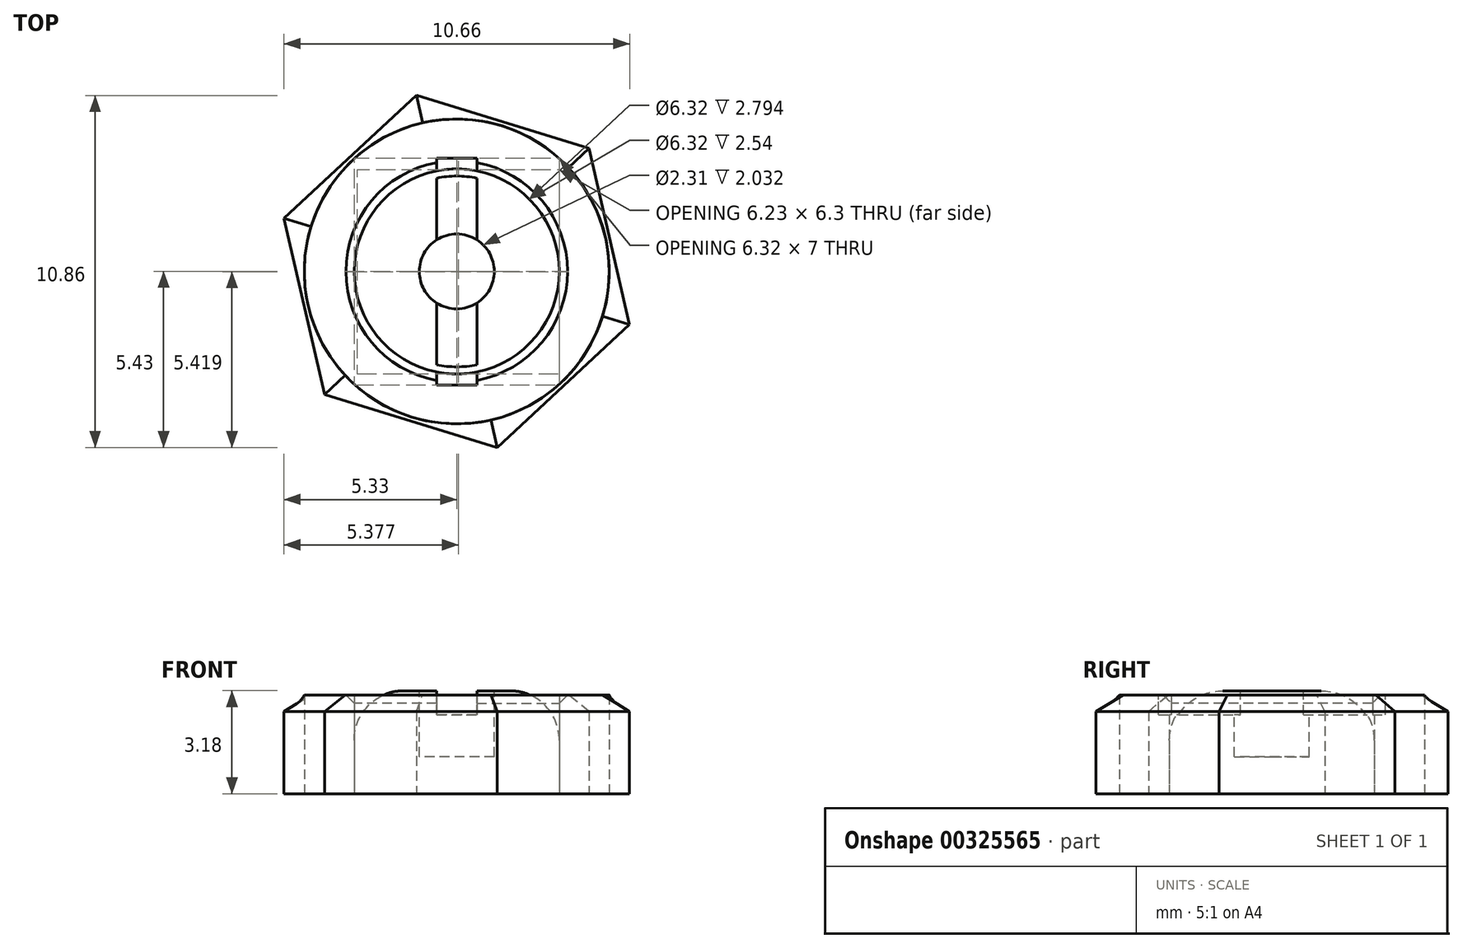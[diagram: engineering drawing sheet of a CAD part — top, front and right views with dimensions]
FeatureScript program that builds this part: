
annotation { "Feature Type Name" : "Feature", "Feature Type Description" : "" }
export const myFeature = defineFeature(function(context is Context, id is Id, definition is map)
    precondition{}
    {
        {
            var Q0;
            Q0=qCreatedBy(makeId("Top.planeOp"),FACE);
            var sketch = newSketch(context, id + "F0", { "sketchPlane" : qUnion([Q0])});
            skCircle(sketch, "E0.cCircle", {"center": v(0, 0) * mm, "radius": 4.83 * mm, "construction": true});
            skLineSegment(sketch, "E0.0", {"start": v(5.33, -1.63) * mm, "end": v(1.25, -5.43) * mm});
            skLineSegment(sketch, "E0.1", {"start": v(1.25, -5.43) * mm, "end": v(-4.08, -3.8) * mm});
            skLineSegment(sketch, "E0.2", {"start": v(-4.08, -3.8) * mm, "end": v(-5.33, 1.63) * mm});
            skLineSegment(sketch, "E0.3", {"start": v(-5.33, 1.63) * mm, "end": v(-1.25, 5.43) * mm});
            skLineSegment(sketch, "E0.4", {"start": v(-1.25, 5.43) * mm, "end": v(4.08, 3.8) * mm});
            skLineSegment(sketch, "E0.5", {"start": v(4.08, 3.8) * mm, "end": v(5.33, -1.63) * mm});
            skPoint(sketch, "E0.0.midPoint", {"position": v(3.29, -3.53) * mm});
            skSolve(sketch);
        }
        {
            var Q0;
            Q0=qCreatedBy(makeId("Top.planeOp"),FACE);
            var sketch = newSketch(context, id + "F1", { "sketchPlane" : qUnion([Q0])});
            skCircle(sketch, "E1", {"center": v(0, 0) * mm, "radius": 4.7 * mm});
            skSolve(sketch);
        }
        {
            var Q0;
            Q0=qCreatedBy(makeId("Top.planeOp"),FACE);
            var sketch = newSketch(context, id + "F2", { "sketchPlane" : qUnion([Q0])});
            skCircle(sketch, "E2", {"center": v(0, 0) * mm, "radius": 3.16 * mm});
            skSolve(sketch);
        }
        {
            var Q0;
            Q0=makeQuery(id+"F0.imprint","IMPRINT",FACE,{"disambiguationData":[TD([[makeQuery(id+"F0.imprint","IMPRINT",EDGE,{"derivedFrom":sQuery(id+"F0.wireOp",EDGE,"E0.0")}),-1.0]])]});
            extrude(context, id + "F3", {"entities" : qUnion([Q0]), "depth" : 2.54 * mm});
        }
        {
            var Q0;
            Q0 = qSketchRegion(id + "F1", true);
            extrude(context, id + "F4", {"entities" : qUnion([Q0]), "depth" : 3.05 * mm});
        }
        {
            var Q0;
            Q0=makeQuery(id+"F3.opExtrude","CAP_FACE",FACE,{"disambiguationData":[OSD([sQuery(id+"F0.wireOp",EDGE,"E0.0"),sQuery(id+"F0.wireOp",EDGE,"E0.1"),sQuery(id+"F0.wireOp",EDGE,"E0.2"),sQuery(id+"F0.wireOp",EDGE,"E0.3"),sQuery(id+"F0.wireOp",EDGE,"E0.4"),sQuery(id+"F0.wireOp",EDGE,"E0.5")])],"isStart":false});
            var Q1;
            Q1=makeQuery(id+"F4.opExtrude","CAP_FACE",FACE,{"disambiguationData":[OSD([sQuery(id+"F1.wireOp",EDGE,"E1")])],"isStart":false});
            loft(context, id + "F5", {"sheetProfilesArray" : [{ "sheetProfileEntities" : qUnion([Q0]) }, { "sheetProfileEntities" : qUnion([Q1]) }]});
        }
        {
            var Q0;
            Q0 = qSketchRegion(id + "F2", true);
            extrude(context, id + "F6", {"entities" : qUnion([Q0]), "operationType" : NewBodyOperationType.REMOVE, "depth" : 5.08 * mm});
        }
        {
            var Q0;
            Q0=makeQuery(id+"F6.boolean.opBoolean","INTERSECT",EDGE,{"derivedFrom":[makeQuery(id+"F4.opExtrude","CAP_FACE",FACE,{"disambiguationData":[OSD([sQuery(id+"F1.wireOp",EDGE,"E1")])],"isStart":false}),makeQuery(id+"F6.opExtrude","SWEPT_FACE",FACE,{"disambiguationData":[OSD([sQuery(id+"F2.wireOp",EDGE,"E2")])]})]});
            chamfer(context, id + "F7", {"entities" : qUnion([Q0]), "width" : 0.25 * mm, "tangentPropagation" : true});
        }
        {
            var Q0;
            Q0 = qSketchRegion(id + "F2", true);
            extrude(context, id + "F8", {"entities" : qUnion([Q0]), "depth" : 3.17 * mm});
        }
        {
            var Q0;
            Q0=makeQuery(id+"F8.opExtrude","CAP_EDGE",EDGE,{"disambiguationData":[OSD([sQuery(id+"F2.wireOp",EDGE,"E2")])],"isStart":false});
            fillet(context, id + "F9", {"entities" : qUnion([Q0]), "radius" : 1.52 * mm, "tangentPropagation" : true, "allowEdgeOverflow" : false});
        }
        {
            var Q0;
            Q0=makeQuery(id+"F8.opExtrude","CAP_FACE",FACE,{"disambiguationData":[OSD([sQuery(id+"F2.wireOp",EDGE,"E2")])],"isStart":false});
            var sketch = newSketch(context, id + "F10", { "sketchPlane" : qUnion([Q0])});
            skLineSegment(sketch, "E3.bottom", {"start": v(0.62, -3.5) * mm, "end": v(-0.62, -3.5) * mm});
            skLineSegment(sketch, "E3.top", {"start": v(0.62, 3.5) * mm, "end": v(-0.62, 3.5) * mm});
            skLineSegment(sketch, "E3.left", {"start": v(0.62, -3.5) * mm, "end": v(0.62, 3.5) * mm});
            skLineSegment(sketch, "E3.right", {"start": v(-0.62, -3.5) * mm, "end": v(-0.62, 3.5) * mm});
            skPoint(sketch, "E3.middle", {"position": v(0, 0) * mm});
            skSolve(sketch);
        }
        {
            var Q0;
            Q0 = qSketchRegion(id + "F10", true);
            extrude(context, id + "F11", {"entities" : qUnion([Q0]), "operationType" : NewBodyOperationType.REMOVE, "oppositeDirection" : true, "depth" : 0.74 * mm});
        }
        {
            var Q0;
            {var subQ0=sQuery(id+"F2.wireOp",EDGE,"E2");Q0=makeQuery(id+"F11.boolean.opBoolean","SPLIT",FACE,{"disambiguationData":[TD([makeQuery(id+"F11.opExtrude","SWEPT_FACE",FACE,{"disambiguationData":[OSD([sQuery(id+"F10.wireOp",EDGE,"E3.left")])]})])],"derivedFrom":makeQuery(id+"F8.opExtrude","CAP_FACE",FACE,{"disambiguationData":[OSD([subQ0])],"isStart":false})});}
            var sketch = newSketch(context, id + "F12", { "sketchPlane" : qUnion([Q0])});
            skCircle(sketch, "E4", {"center": v(0, 0) * mm, "radius": 1.16 * mm});
            skSolve(sketch);
        }
        {
            var Q0;
            Q0 = qSketchRegion(id + "F12", true);
            extrude(context, id + "F13", {"entities" : qUnion([Q0]), "operationType" : NewBodyOperationType.REMOVE, "oppositeDirection" : true, "depth" : 2.03 * mm});
        }
    });
